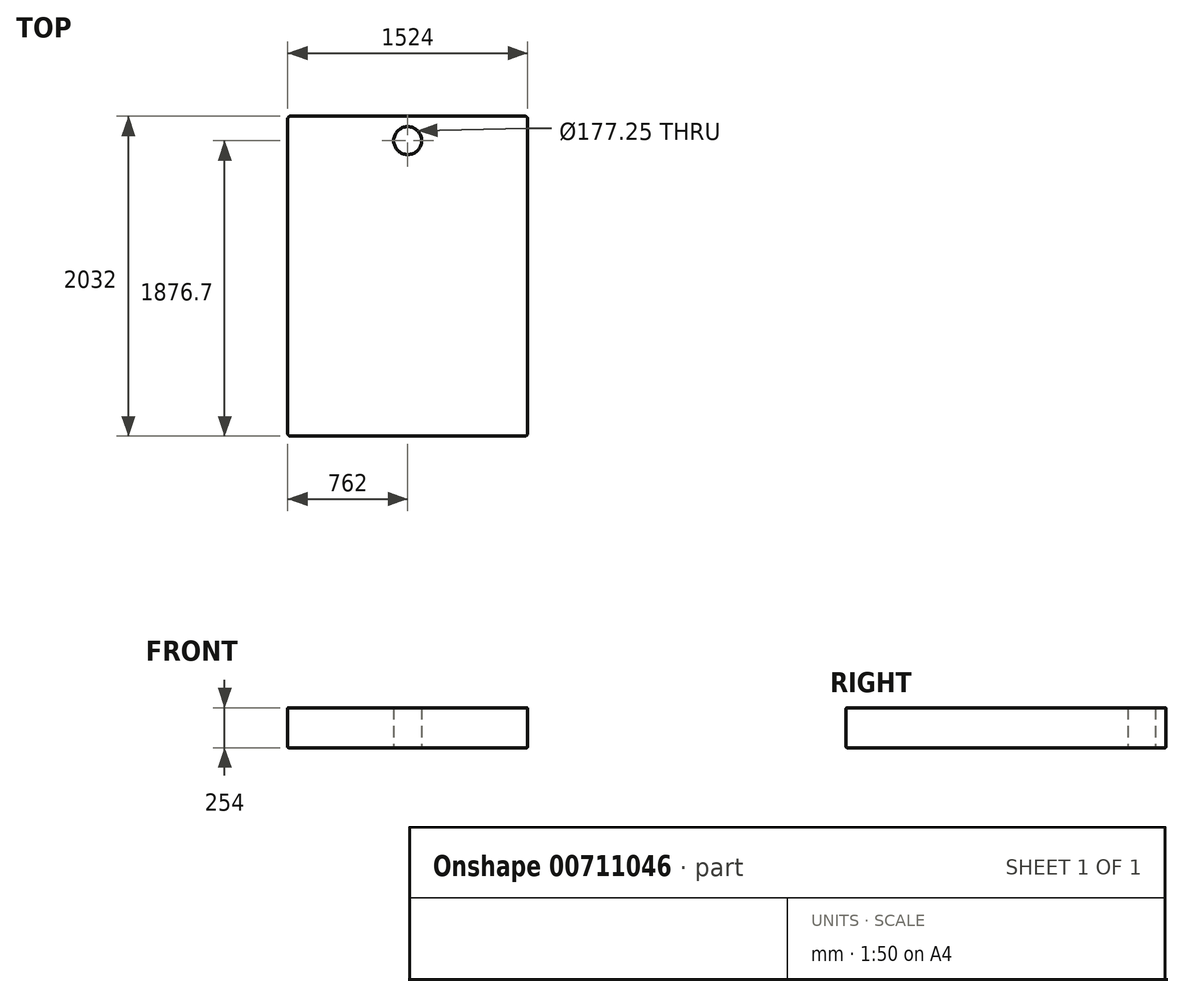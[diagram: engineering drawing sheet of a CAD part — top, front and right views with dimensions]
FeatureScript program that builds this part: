
annotation { "Feature Type Name" : "Feature", "Feature Type Description" : "" }
export const myFeature = defineFeature(function(context is Context, id is Id, definition is map)
    precondition{}
    {
        {
            var Q0;
            Q0=qCreatedBy(makeId("Top.planeOp"),FACE);
            var sketch = newSketch(context, id + "F0", { "sketchPlane" : qUnion([Q0])});
            skLineSegment(sketch, "E0.bottom", {"start": v(762, 1016) * mm, "end": v(-762, 1016) * mm});
            skLineSegment(sketch, "E0.top", {"start": v(762, -1016) * mm, "end": v(-762, -1016) * mm});
            skLineSegment(sketch, "E0.left", {"start": v(762, 1016) * mm, "end": v(762, -1016) * mm});
            skLineSegment(sketch, "E0.right", {"start": v(-762, 1016) * mm, "end": v(-762, -1016) * mm});
            skPoint(sketch, "E0.middle", {"position": v(0, 0) * mm});
            skCircle(sketch, "E1", {"center": v(0, 860.7) * mm, "radius": 88.63 * mm});
            skSolve(sketch);
        }
        {
            var Q0;
            Q0 = qSketchRegion(id + "F0", true);
            extrude(context, id + "F1", {"entities" : qUnion([Q0]), "depth" : 254 * mm, "offsetDistance" : 25.4 * mm});
        }
        {
            var Q0;
            Q0=makeQuery(id+"F1.opExtrude","CAP_EDGE",EDGE,{"disambiguationData":[OSD([sQuery(id+"F0.wireOp",EDGE,"E0.right")])],"isStart":false});
            var Q1;
            Q1=makeQuery(id+"F1.opExtrude","CAP_EDGE",EDGE,{"disambiguationData":[OSD([sQuery(id+"F0.wireOp",EDGE,"E0.top")])],"isStart":false});
            var Q2;
            Q2=makeQuery(id+"F1.opExtrude","CAP_EDGE",EDGE,{"disambiguationData":[OSD([sQuery(id+"F0.wireOp",EDGE,"E0.left")])],"isStart":false});
            var Q3;
            Q3=makeQuery(id+"F1.opExtrude","CAP_EDGE",EDGE,{"disambiguationData":[OSD([sQuery(id+"F0.wireOp",EDGE,"E0.bottom")])],"isStart":false});
            var Q4;
            Q4=makeQuery(id+"F1.opExtrude","CAP_EDGE",EDGE,{"disambiguationData":[OSD([sQuery(id+"F0.wireOp",EDGE,"E0.bottom")])],"isStart":true});
            var Q5;
            Q5=makeQuery(id+"F1.opExtrude","CAP_EDGE",EDGE,{"disambiguationData":[OSD([sQuery(id+"F0.wireOp",EDGE,"E0.left")])],"isStart":true});
            var Q6;
            Q6=makeQuery(id+"F1.opExtrude","CAP_EDGE",EDGE,{"disambiguationData":[OSD([sQuery(id+"F0.wireOp",EDGE,"E0.top")])],"isStart":true});
            var Q7;
            Q7=makeQuery(id+"F1.opExtrude","CAP_EDGE",EDGE,{"disambiguationData":[OSD([sQuery(id+"F0.wireOp",EDGE,"E0.right")])],"isStart":true});
            fillet(context, id + "F2", {"entities" : qUnion([Q0, Q1, Q2, Q3, Q4, Q5, Q6, Q7]), "radius" : 5.08 * mm, "tangentPropagation" : true, "allowEdgeOverflow" : false});
        }
        {
            var Q0;
            Q0=makeQuery(id+"F1.opExtrude","SWEPT_EDGE",EDGE,{"disambiguationData":[OSD([sQuery(id+"F0.wireOp",EDGE,"E0.bottom"),sQuery(id+"F0.wireOp",EDGE,"E0.left")])]});
            var Q1;
            Q1=makeQuery(id+"F1.opExtrude","SWEPT_EDGE",EDGE,{"disambiguationData":[OSD([sQuery(id+"F0.wireOp",EDGE,"E0.top"),sQuery(id+"F0.wireOp",EDGE,"E0.left")])]});
            var Q2;
            Q2=makeQuery(id+"F1.opExtrude","SWEPT_EDGE",EDGE,{"disambiguationData":[OSD([sQuery(id+"F0.wireOp",EDGE,"E0.top"),sQuery(id+"F0.wireOp",EDGE,"E0.right")])]});
            var Q3;
            Q3=makeQuery(id+"F1.opExtrude","SWEPT_EDGE",EDGE,{"disambiguationData":[OSD([sQuery(id+"F0.wireOp",EDGE,"E0.bottom"),sQuery(id+"F0.wireOp",EDGE,"E0.right")])]});
            fillet(context, id + "F3", {"entities" : qUnion([Q0, Q1, Q2, Q3]), "radius" : 19.05 * mm, "tangentPropagation" : true, "allowEdgeOverflow" : false});
        }
    });
